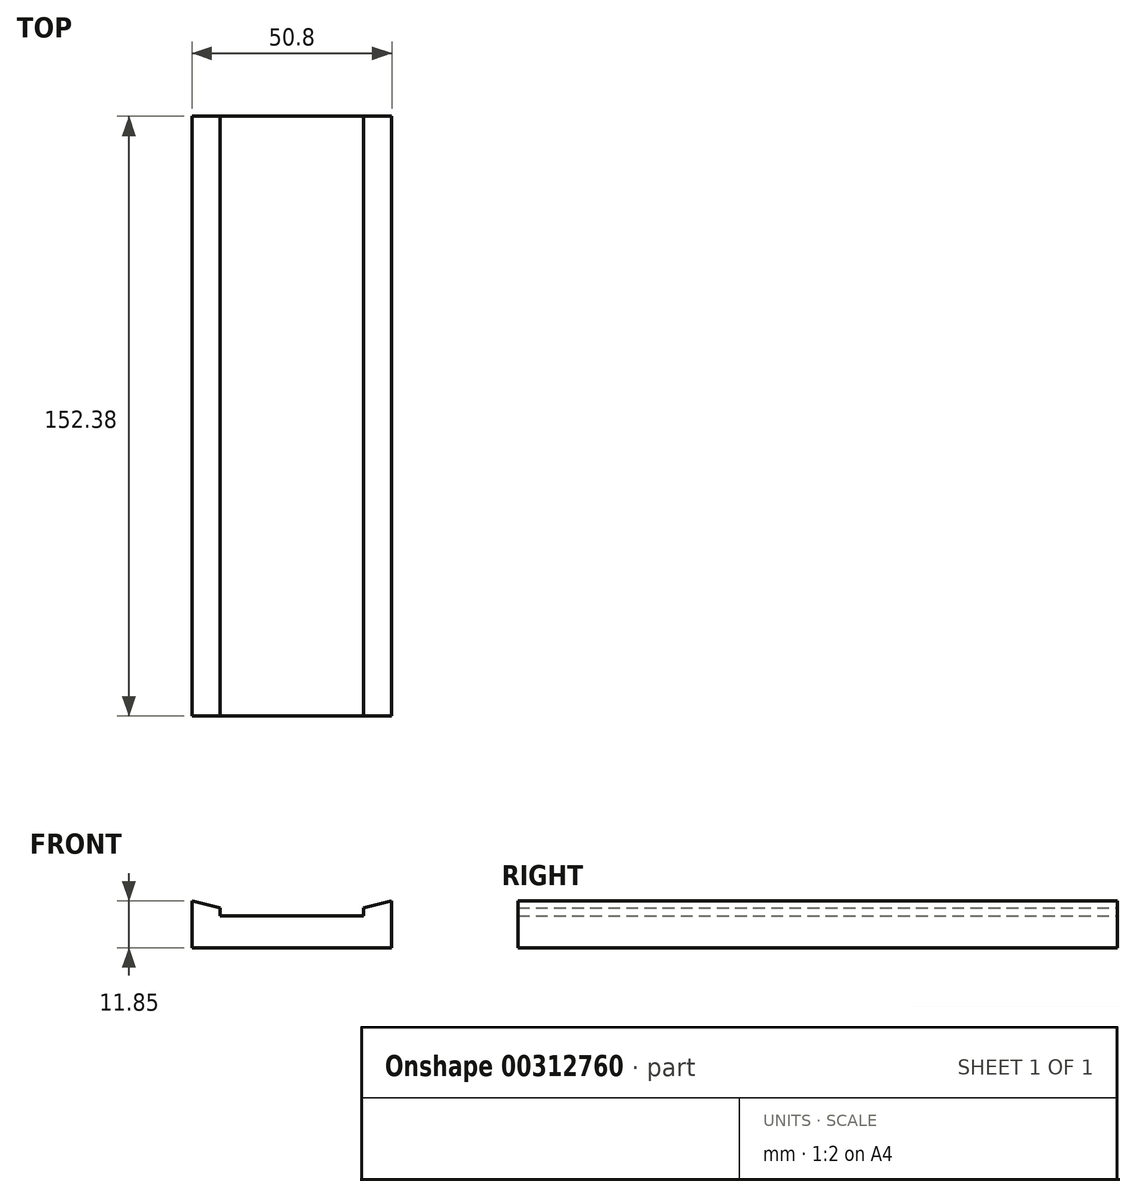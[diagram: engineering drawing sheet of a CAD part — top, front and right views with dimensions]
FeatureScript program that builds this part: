
annotation { "Feature Type Name" : "Feature", "Feature Type Description" : "" }
export const myFeature = defineFeature(function(context is Context, id is Id, definition is map)
    precondition{}
    {
        {
            var Q0;
            Q0=qCreatedBy(makeId("Front.planeOp"),FACE);
            var sketch = newSketch(context, id + "F0", { "sketchPlane" : qUnion([Q0])});
            skLineSegment(sketch, "E0.bottom", {"start": v(0, 0) * mm, "end": v(38.1, 0) * mm});
            skLineSegment(sketch, "E0.left", {"start": v(0, 0) * mm, "end": v(0, 12.2) * mm});
            skLineSegment(sketch, "E0.right", {"start": v(38.1, 0) * mm, "end": v(38.1, 17.78) * mm});
            skLineSegment(sketch, "E1", {"start": v(38.1, 17.78) * mm, "end": v(27.3, 15.24) * mm});
            skLineSegment(sketch, "E2", {"start": v(27.3, 15.24) * mm, "end": v(27.3, 12.2) * mm});
            skLineSegment(sketch, "E3", {"start": v(27.3, 12.2) * mm, "end": v(0, 12.2) * mm});
            skLineSegment(sketch, "E4.MirrorCS", {"start": v(-27.3, 12.2) * mm, "end": v(0, 12.2) * mm});
            skLineSegment(sketch, "E5.MirrorCS", {"start": v(-27.3, 15.24) * mm, "end": v(-27.3, 12.2) * mm});
            skLineSegment(sketch, "E6.MirrorCS", {"start": v(-38.1, 17.78) * mm, "end": v(-27.3, 15.24) * mm});
            skLineSegment(sketch, "E7.MirrorCS", {"start": v(-38.1, 0) * mm, "end": v(-38.1, 17.78) * mm});
            skLineSegment(sketch, "E8.MirrorCS", {"start": v(0, 0) * mm, "end": v(-38.1, 0) * mm});
            skSolve(sketch);
        }
        {
            var Q0;
            Q0 = qSketchRegion(id + "F0", true);
            extrude(context, id + "F1", {"entities" : qUnion([Q0]), "depth" : 228.6 * mm});
        }
        {
            var Q0;
            Q0=makeQuery(id+"F1.opExtrude","SWEPT_BODY",BODY,{"disambiguationData":[OSD([sQuery(id+"F0.wireOp",EDGE,"E0.bottom"),sQuery(id+"F0.wireOp",EDGE,"E0.right"),sQuery(id+"F0.wireOp",EDGE,"E1"),sQuery(id+"F0.wireOp",EDGE,"E2"),sQuery(id+"F0.wireOp",EDGE,"E3"),sQuery(id+"F0.wireOp",EDGE,"E4.MirrorCS"),sQuery(id+"F0.wireOp",EDGE,"E5.MirrorCS"),sQuery(id+"F0.wireOp",EDGE,"E6.MirrorCS"),sQuery(id+"F0.wireOp",EDGE,"E7.MirrorCS"),sQuery(id+"F0.wireOp",EDGE,"E8.MirrorCS")])]});
            var Q1;
            Q1=qCreatedBy(makeId("Origin.pointOp"),VERTEX);
            transform(context, id + "F2", {"entities" : qUnion([Q0]), "transformType" : TransformType.SCALE_UNIFORMLY, "scale" : .6666, "scalePoint" : qUnion([Q1]), "makeCopy" : false});
        }
    });
